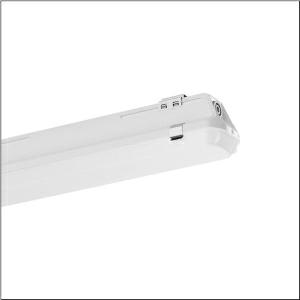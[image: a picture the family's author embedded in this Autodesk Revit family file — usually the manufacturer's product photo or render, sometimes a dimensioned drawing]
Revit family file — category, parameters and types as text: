
# Revit family: monsun_r__21_51fb20dp460b_2c2a
name_source: partatom
category: Lighting Fixtures
units: mm (PartAtom-declared; Revit-internal decimal feet)

## family parameters
Cut with Voids When Loaded = No
Host = Face
Light Source = No
Part Type = Normal
Room Calculation Point = No
Round Connector Dimension = Use Diameter
Shared = No

## types (1)
- --- (1 x LED, 5460 lm, 39.4 W, 4000K)
    Apparent Load = 39 VA
    CIE Flux Codes = 45 75 93 94 100
    Color Rendering = 80
    Color Temperature = 4000K
    Default Elevation = 1800 mm
    Description = Monsun® 21, damp-proof luminaire, chain hanger, primary optical cover: enclosure, of PC, light emission: direct distribution, primary light characteristic: symmetric, installation type: suspended mounting, surface-mounted, horizontal mounting, vertical mounting, LED, rated luminous flux: 5.460lm, luminous efficacy: 139lm/W, light colour: 840, colour temperature: 4000K, control gear: ECG DALI, with terminal, 5-pole, max. 2.5mm², mains connection: 220..240V, AC, 50/60Hz, rated input power: 39W, housing, of glass-fibre reinforced polyester, uncoated, bright grey, incl. chain hanger, length: 1.590mm, width: 90mm, height: 88mm, clip for enclosure, of stainless steel (V2A), ceiling mounting element, of stainless steel (V2A), chain hanger, of stainless steel (V2A), protection rating (complete): IP66, insulation class (complete): insulation class I (protective earthing), certification: CE, ENEC, VDE, UKCA, protection symbol: D, impact resistance: IK08, permissible operating ambient temperature: -25..+35°C, standard: EN 50419, EN 60598-2-1, corresponds to IFS (International Featured Standards) requirements for safety and quality in the food industry, for indoor or canopied outdoor use, no direct snow, no direct sun, no direct rain, contact your sales advisor before using the luminaires in applications with unclear chemical exposure, large temperature fluctuations or condensation-forming humidity, LABS conformity tested according to VDMA 24364:2018-05, packaging unit: 1 piece
    Height = 89 mm
    Lamp = 1 x LED
    Lamp Light Flux = 5460 lm
    Lamp Power = 39.4 W
    Lamp count = 1
    Length = 1590 mm
    Luminous efficacy = 139 lm/W
    Manufacturer = Siteco
    ModVariant = No
    Model = 51FB20DP460B
    Mounting Place = Ceiling
    Mounting Type = Surface mounted
    Number of Poles = 1
    OnlyDefault = Yes
    Power Factor = 1
    Product Name = Monsun® 21
    Product group = damp-proof luminaire
    ProductGroupID = 301
    Protection Class = Protection class I
    Protection Degree = IP 66
    RLX_Detail_Level = 1
    RLX_Emergency_Light_Flux = 0 lm
    RLX_Emergency_Type = 0
    RLX_Emergency_Type_DB = No
    RlxData = <blob elided: 92133 chars, md5=76304274>
    Socket = socket
    Standby Power = 0 W
    System Light Flux = 5460 lm
    System Power = 39 W
    Type Comments = factory setting: luminous flux: 100 % | dim-lin: 254 | 261 mA
    Type Image = l_1006717.jpg
    URL = http://relux.com
    VarID = @adj_152145
    Voltage = 0 V
    Weight = 0.00 kg
    Width = 90 mm

## geometry (parser evidence)
native form markers: Blend x4, Sweep x15
no freeform markers — native parametric forms only
